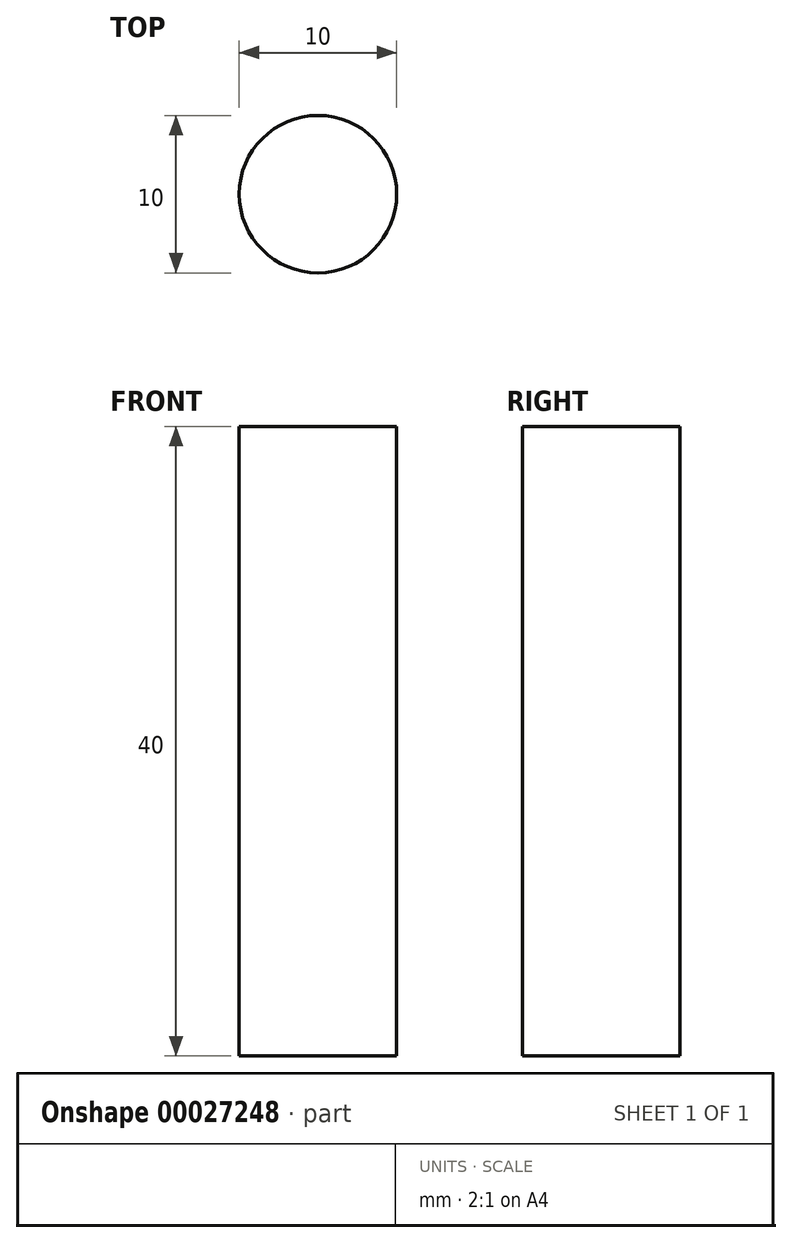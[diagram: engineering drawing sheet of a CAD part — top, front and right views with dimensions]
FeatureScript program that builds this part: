
annotation { "Feature Type Name" : "Feature", "Feature Type Description" : "" }
export const myFeature = defineFeature(function(context is Context, id is Id, definition is map)
    precondition{}
    {
        {
            var Q0;
            Q0=qCreatedBy(makeId("Top.planeOp"),FACE);
            var sketch = newSketch(context, id + "F0", { "sketchPlane" : qUnion([Q0])});
            skCircle(sketch, "E0", {"center": v(-16.85, -0.46) * mm, "radius": 5 * mm});
            skSolve(sketch);
        }
        {
            var Q0;
            Q0 = qSketchRegion(id + "F0", true);
            extrude(context, id + "F1", {"entities" : qUnion([Q0]), "depth" : 40 * mm});
        }
    });
